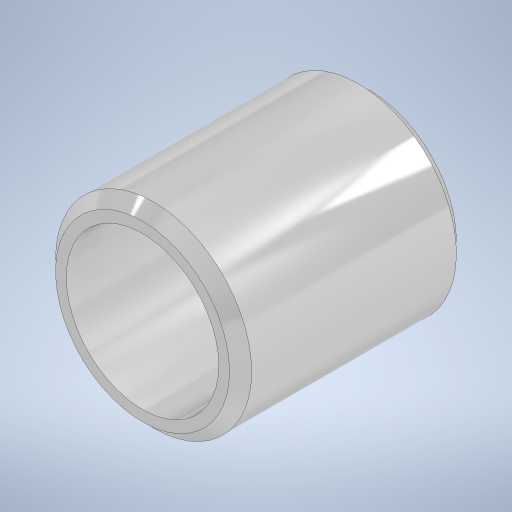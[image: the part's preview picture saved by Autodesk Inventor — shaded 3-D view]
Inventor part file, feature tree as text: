
AUTODESK INVENTOR PART (.ipt)
format: ipt  version: 2023 (Build 270158000, 158)  size: 247,296 bytes
history: native  units: in
note: dims shown in document units (in); Inventor stores cm internally (conversion verified against a paired STEP export)
features: extrude x1, chamfer x1, sketch x1
ambient origin geometry x8: Origin, YZ Plane, XZ Plane, XY Plane, X Axis, Y Axis, Z Axis, Center Point
bodies: Solid1 (feature_tree)
feature tree (3):
  extrude  "Extrusion1"  Depth=0.41in
  chamfer  "Chamfer1"  Distance=0.41in
  sketch  "Sketch1"  dims[d0=0.2756in d1=0.0394in d2=0.41in d3=0.0in d4=0.02in d5=0.125in d6=45.0deg]
